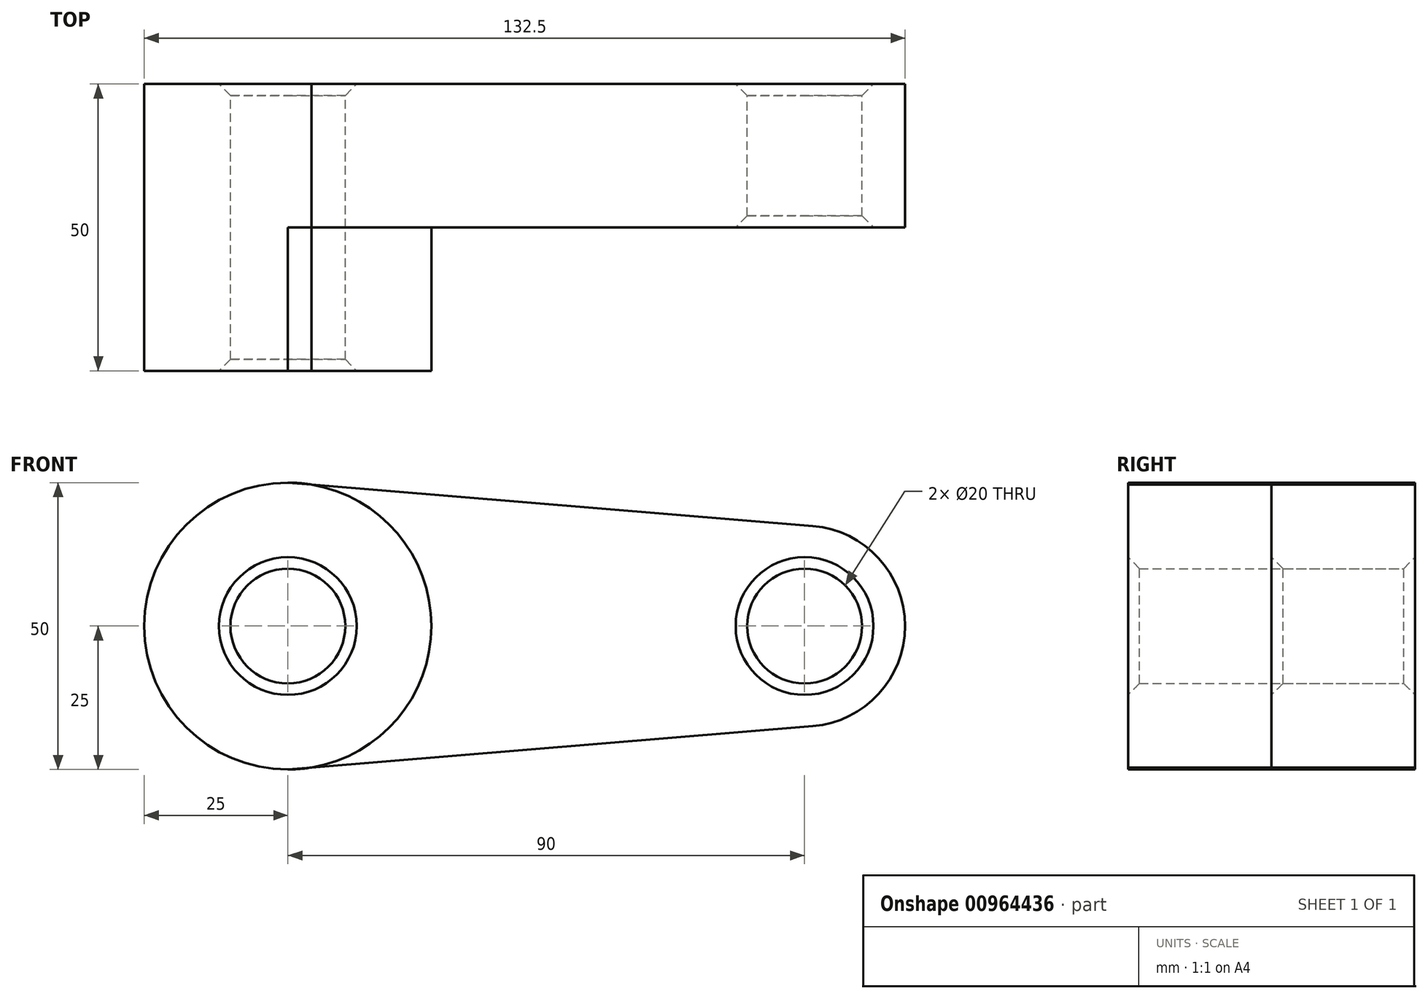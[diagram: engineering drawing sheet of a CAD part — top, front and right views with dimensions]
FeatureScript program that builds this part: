
annotation { "Feature Type Name" : "Feature", "Feature Type Description" : "" }
export const myFeature = defineFeature(function(context is Context, id is Id, definition is map)
    precondition{}
    {
        {
            var Q0;
            Q0=qCreatedBy(makeId("Front.planeOp"),FACE);
            var sketch = newSketch(context, id + "F0", { "sketchPlane" : qUnion([Q0])});
            skCircle(sketch, "E0", {"center": v(0, 0) * mm, "radius": 25 * mm});
            skCircle(sketch, "E1", {"center": v(90, 0) * mm, "radius": 17.5 * mm});
            skLineSegment(sketch, "E2", {"start": v(0, 25) * mm, "end": v(91.44, 17.44) * mm});
            skLineSegment(sketch, "E3", {"start": v(0, -25) * mm, "end": v(91.44, -17.44) * mm});
            skCircle(sketch, "E4", {"center": v(0, 0) * mm, "radius": 10 * mm});
            skCircle(sketch, "E5", {"center": v(90, 0) * mm, "radius": 10 * mm});
            skSolve(sketch);
        }
        {
            var Q0;
            Q0 = qSketchRegion(id + "F0", true);
            extrude(context, id + "F1", {"entities" : qUnion([Q0]), "depth" : 25 * mm, "offsetDistance" : 25 * mm});
        }
        {
            var Q0;
            Q0=makeQuery(id+"F0.imprint","IMPRINT",FACE,{"disambiguationData":[TD([[makeQuery(id+"F0.imprint","IMPRINT",EDGE,{"derivedFrom":sQuery(id+"F0.wireOp",EDGE,"E4")}),-1.0]])]});
            extrude(context, id + "F2", {"entities" : qUnion([Q0]), "operationType" : NewBodyOperationType.ADD, "depth" : 50 * mm, "offsetDistance" : 25 * mm});
        }
        {
            var Q0;
            {var subQ0=sQuery(id+"F0.wireOp",EDGE,"E4");Q0=makeQuery(id+"F2.boolean.opBoolean","MERGE",FACE,{"derivedFrom":[makeQuery(id+"F1.opExtrude","SWEPT_FACE",FACE,{"disambiguationData":[OSD([subQ0])]}),makeQuery(id+"F2.opExtrude","SWEPT_FACE",FACE,{"disambiguationData":[OSD([subQ0])]})]});}
            var Q1;
            {var subQ0=sQuery(id+"F0.wireOp",EDGE,"E0");Q1=makeQuery(id+"F2.opExtrude","CAP_EDGE",EDGE,{"disambiguationData":[OSD([subQ0]),TDD([makeQuery(id+"F0.imprint","IMPRINT",EDGE,{"disambiguationData":[TD([[makeQuery(id+"F0.imprint","INTERSECT",VERTEX,{"disambiguationData":[OD(0.0)],"derivedFrom":[subQ0,sQuery(id+"F0.wireOp",EDGE,"E2")]}),-1.0]])],"derivedFrom":subQ0})])],"isStart":false});}
            var Q2;
            Q2=makeQuery(id+"F1.opExtrude","SWEPT_FACE",FACE,{"disambiguationData":[OSD([sQuery(id+"F0.wireOp",EDGE,"E5")])]});
            chamfer(context, id + "F3", {"entities" : qUnion([Q0, Q1, Q2]), "width" : 2 * mm, "tangentPropagation" : true});
        }
    });
